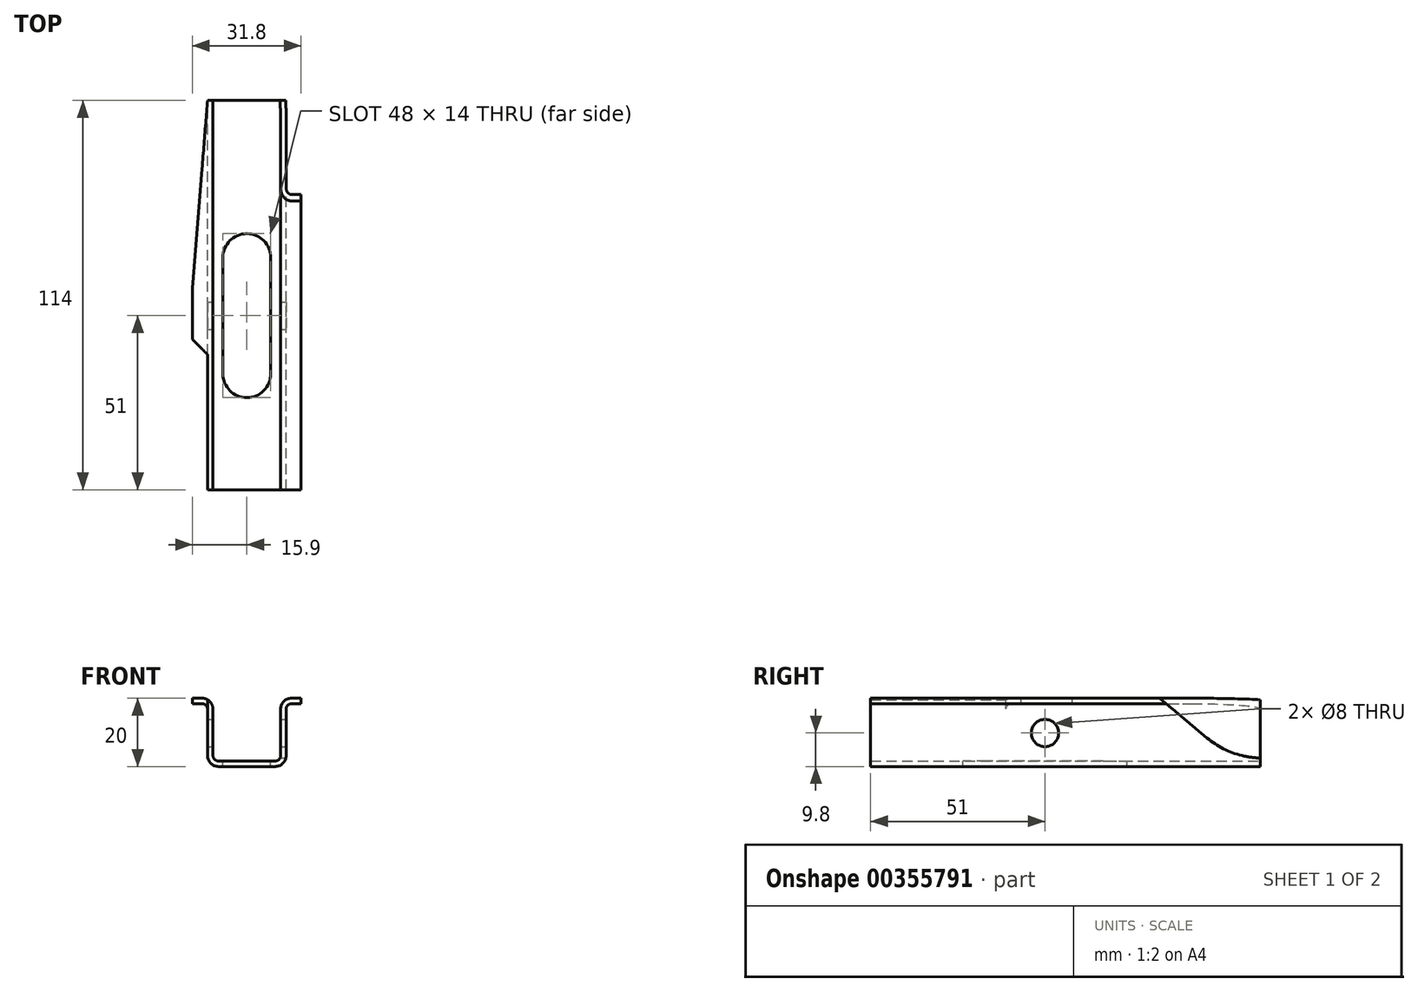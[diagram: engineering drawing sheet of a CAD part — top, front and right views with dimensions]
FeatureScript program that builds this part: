
annotation { "Feature Type Name" : "Feature", "Feature Type Description" : "" }
export const myFeature = defineFeature(function(context is Context, id is Id, definition is map)
    precondition{}
    {
        {
            var Q0;
            Q0=qCreatedBy(makeId("Front.planeOp"),FACE);
            var sketch = newSketch(context, id + "F0", { "sketchPlane" : qUnion([Q0])});
            skLineSegment(sketch, "E0", {"start": v(-8.3, 0) * mm, "end": v(0, 0) * mm});
            skLineSegment(sketch, "E1", {"start": v(-8.3, 1.6) * mm, "end": v(0, 1.6) * mm});
            skLineSegment(sketch, "E2", {"start": v(-11.5, 3.2) * mm, "end": v(-11.5, 16.8) * mm});
            skLineSegment(sketch, "E3", {"start": v(-9.9, 3.2) * mm, "end": v(-9.9, 16.8) * mm});
            skLineSegment(sketch, "E4", {"start": v(-13.1, 20) * mm, "end": v(-15.9, 20) * mm});
            skLineSegment(sketch, "E5", {"start": v(-15.9, 20) * mm, "end": v(-15.9, 18.4) * mm});
            skPoint(sketch, "E6.endSnap0", {"position": v(-15.9, 18.08) * mm});
            skPoint(sketch, "E7.orphan", {"position": v(-26.3, 18.08) * mm});
            skPoint(sketch, "E8.orphan", {"position": v(-15.9, 16.17) * mm});
            skLineSegment(sketch, "E9", {"start": v(-13.1, 18.4) * mm, "end": v(-15.9, 18.4) * mm});
            skPoint(sketch, "E10.visualSharp", {"position": v(-11.5, 18.4) * mm});
            skArc(sketch, "E10.filletArc", {"start": v(-11.5, 16.8) * mm, "mid": v(-11.97, 17.93) * mm, "end": v(-13.1, 18.4) * mm});
            skPoint(sketch, "E11.visualSharp", {"position": v(-9.9, 1.6) * mm});
            skArc(sketch, "E11.filletArc", {"start": v(-9.9, 3.2) * mm, "mid": v(-9.43, 2.07) * mm, "end": v(-8.3, 1.6) * mm});
            skPoint(sketch, "E12.visualSharp", {"position": v(-9.9, 20) * mm});
            skArc(sketch, "E12.filletArc", {"start": v(-9.9, 16.8) * mm, "mid": v(-10.84, 19.06) * mm, "end": v(-13.1, 20) * mm});
            skPoint(sketch, "E13.visualSharp", {"position": v(-11.5, 0) * mm});
            skArc(sketch, "E13.filletArc", {"start": v(-11.5, 3.2) * mm, "mid": v(-10.56, 0.94) * mm, "end": v(-8.3, 0) * mm});
            skLineSegment(sketch, "E14", {"start": v(0, 0) * mm, "end": v(0, 25.46) * mm, "construction": true});
            skLineSegment(sketch, "E15.MirrorCS", {"start": v(15.9, 20) * mm, "end": v(15.9, 18.4) * mm});
            skPoint(sketch, "E16.MirrorP", {"position": v(26.3, 18.08) * mm});
            skArc(sketch, "E17.MirrorCS", {"start": v(9.9, 3.2) * mm, "mid": v(9.43, 2.07) * mm, "end": v(8.3, 1.6) * mm});
            skArc(sketch, "E18.MirrorCS", {"start": v(11.5, 16.8) * mm, "mid": v(11.97, 17.93) * mm, "end": v(13.1, 18.4) * mm});
            skLineSegment(sketch, "E19.MirrorCS", {"start": v(8.3, 0) * mm, "end": v(0, 0) * mm});
            skLineSegment(sketch, "E20.MirrorCS", {"start": v(8.3, 1.6) * mm, "end": v(0, 1.6) * mm});
            skPoint(sketch, "E21.MirrorP", {"position": v(9.9, 1.6) * mm});
            skLineSegment(sketch, "E22.MirrorCS", {"start": v(11.5, 3.2) * mm, "end": v(11.5, 16.8) * mm});
            skLineSegment(sketch, "E23.MirrorCS", {"start": v(9.9, 3.2) * mm, "end": v(9.9, 16.8) * mm});
            skPoint(sketch, "E24.MirrorP", {"position": v(15.9, 18.08) * mm});
            skPoint(sketch, "E25.MirrorP", {"position": v(15.9, 16.17) * mm});
            skPoint(sketch, "E26.MirrorP", {"position": v(11.5, 18.4) * mm});
            skArc(sketch, "E27.MirrorCS", {"start": v(11.5, 3.2) * mm, "mid": v(10.56, 0.94) * mm, "end": v(8.3, 0) * mm});
            skLineSegment(sketch, "E28.MirrorCS", {"start": v(13.1, 18.4) * mm, "end": v(15.9, 18.4) * mm});
            skArc(sketch, "E29.MirrorCS", {"start": v(9.9, 16.8) * mm, "mid": v(10.84, 19.06) * mm, "end": v(13.1, 20) * mm});
            skPoint(sketch, "E30.MirrorP", {"position": v(9.9, 20) * mm});
            skPoint(sketch, "E31.MirrorP", {"position": v(11.5, 0) * mm});
            skLineSegment(sketch, "E32.MirrorCS", {"start": v(13.1, 20) * mm, "end": v(15.9, 20) * mm});
            skSolve(sketch);
        }
        {
            var Q0;
            Q0=qSketchRegion(id+"F0",true);
            extrude(context, id + "F1", {"entities" : qUnion([Q0]), "depth" : 114 * mm});
        }
        {
            var Q0;
            Q0=makeQuery(id+"F1.opExtrude","SWEPT_FACE",FACE,{"disambiguationData":[OSD([sQuery(id+"F0.wireOp",EDGE,"E1"),sQuery(id+"F0.wireOp",EDGE,"E20.MirrorCS")])]});
            var sketch = newSketch(context, id + "F2", { "sketchPlane" : qUnion([Q0])});
            skLineSegment(sketch, "E33.bottom", {"start": v(7, -46) * mm, "end": v(-7, -46) * mm});
            skLineSegment(sketch, "E33.top", {"start": v(7, -80) * mm, "end": v(-7, -80) * mm});
            skLineSegment(sketch, "E33.left", {"start": v(7, -46) * mm, "end": v(7, -80) * mm});
            skLineSegment(sketch, "E33.right", {"start": v(-7, -46) * mm, "end": v(-7, -80) * mm});
            skPoint(sketch, "E33.middle", {"position": v(0, -63) * mm});
            skLineSegment(sketch, "E34", {"start": v(0, 0) * mm, "end": v(0, -144.93) * mm, "construction": true});
            skCircle(sketch, "E35", {"center": v(0, -46) * mm, "radius": 7 * mm});
            skCircle(sketch, "E36", {"center": v(0, -80) * mm, "radius": 7 * mm});
            skSolve(sketch);
        }
        {
            var Q0;
            Q0=qSketchRegion(id+"F2",true);
            extrude(context, id + "F3", {"entities" : qUnion([Q0]), "operationType" : NewBodyOperationType.REMOVE, "oppositeDirection" : true, "depth" : 25 * mm});
        }
        {
            var Q0;
            Q0=makeQuery(id+"F1.opExtrude","SWEPT_FACE",FACE,{"disambiguationData":[OSD([sQuery(id+"F0.wireOp",EDGE,"E4")])]});
            var sketch = newSketch(context, id + "F4", { "sketchPlane" : qUnion([Q0])});
            skLineSegment(sketch, "E37", {"start": v(-15.9, 0) * mm, "end": v(-11.5, 0) * mm});
            skPoint(sketch, "E37.endSnap0", {"position": v(-14.5, 0) * mm});
            skLineSegment(sketch, "E38", {"start": v(-11.5, 0) * mm, "end": v(-15.9, -55) * mm});
            skLineSegment(sketch, "E39", {"start": v(-15.9, -55) * mm, "end": v(-15.9, 0) * mm});
            skLineSegment(sketch, "E40", {"start": v(-15.9, -70) * mm, "end": v(-11.5, -74.4) * mm});
            skLineSegment(sketch, "E41", {"start": v(-11.5, -74.4) * mm, "end": v(-11.5, -114) * mm});
            skLineSegment(sketch, "E42", {"start": v(-11.5, -114) * mm, "end": v(-15.9, -114) * mm});
            skLineSegment(sketch, "E43", {"start": v(-15.9, -114) * mm, "end": v(-15.9, -70) * mm});
            skSolve(sketch);
        }
        {
            var Q0;
            Q0=qSketchRegion(id+"F4",true);
            extrude(context, id + "F5", {"entities" : qUnion([Q0]), "operationType" : NewBodyOperationType.REMOVE, "oppositeDirection" : true, "depth" : 5 * mm});
        }
        {
            var Q0;
            Q0=makeQuery(id+"F1.opExtrude","SWEPT_FACE",FACE,{"disambiguationData":[OSD([sQuery(id+"F0.wireOp",EDGE,"E22.MirrorCS")])]});
            var sketch = newSketch(context, id + "F6", { "sketchPlane" : qUnion([Q0])});
            skCircle(sketch, "E44", {"center": v(-63, 9.8) * mm, "radius": 4 * mm});
            skSolve(sketch);
        }
        {
            var Q0;
            Q0=qSketchRegion(id+"F6",true);
            extrude(context, id + "F7", {"entities" : qUnion([Q0]), "operationType" : NewBodyOperationType.REMOVE, "oppositeDirection" : true, "depth" : 30 * mm});
        }
        {
            var Q0;
            Q0=makeQuery(id+"F1.opExtrude","SWEPT_FACE",FACE,{"disambiguationData":[OSD([sQuery(id+"F0.wireOp",EDGE,"E22.MirrorCS")])]});
            var sketch = newSketch(context, id + "F8", { "sketchPlane" : qUnion([Q0])});
            skArc(sketch, "E45", {"start": v(-15.57, 8.35) * mm, "mid": v(-8.05, 4) * mm, "end": v(0.5, 2.5) * mm});
            skLineSegment(sketch, "E46", {"start": v(-15.57, 8.35) * mm, "end": v(-38.4, 27.5) * mm});
            skLineSegment(sketch, "E47", {"start": v(0.5, 2.5) * mm, "end": v(5, 2.5) * mm});
            skLineSegment(sketch, "E48", {"start": v(5, 2.5) * mm, "end": v(5, 27.5) * mm});
            skLineSegment(sketch, "E49", {"start": v(-38.4, 27.5) * mm, "end": v(5, 27.5) * mm});
            skSolve(sketch);
        }
        {
            var Q0;
            Q0=qSketchRegion(id+"F8",true);
            extrude(context, id + "F9", {"entities" : qUnion([Q0]), "operationType" : NewBodyOperationType.REMOVE, "endBound" : BoundingType.SYMMETRIC, "oppositeDirection" : true, "depth" : 10 * mm});
        }
    });
